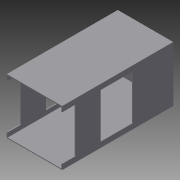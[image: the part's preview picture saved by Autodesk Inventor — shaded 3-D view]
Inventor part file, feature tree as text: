
AUTODESK INVENTOR PART (.ipt)
format: ipt  version: 2015 SP1 (Build 190203100, 203)  size: 112,128 bytes
history: native  units: mm
features: extrude x3, sketch x3, projected_geometry x2
ambient origin geometry x8: Origin, YZ Plane, XZ Plane, XY Plane, X Axis, Y Axis, Z Axis, Center Point
bodies: Solid1 (feature_tree)
feature tree (8):
  extrude  "Extrusion1"  Depth=3.175mm
  extrude  "Extrusion2"  Depth=3.175mm TaperAngle=0.0deg
  extrude  "Extrusion3"  Depth=20.0mm
  sketch  "Sketch1"  dims[d0=200.0mm d1=3.175mm]
  sketch  "Sketch2"  dims[d2=410.0mm d3=0.0mm d4=3.175mm d5=0.0mm]
  projected_geometry  "Projected Loop1"
  sketch  "Sketch3"  dims[d6=50.0mm d7=20.0mm d8=20.0mm d9=150.0mm d10=3.175mm d11=0.0mm d12=120.0mm]
  projected_geometry  "Projected Loop2"
